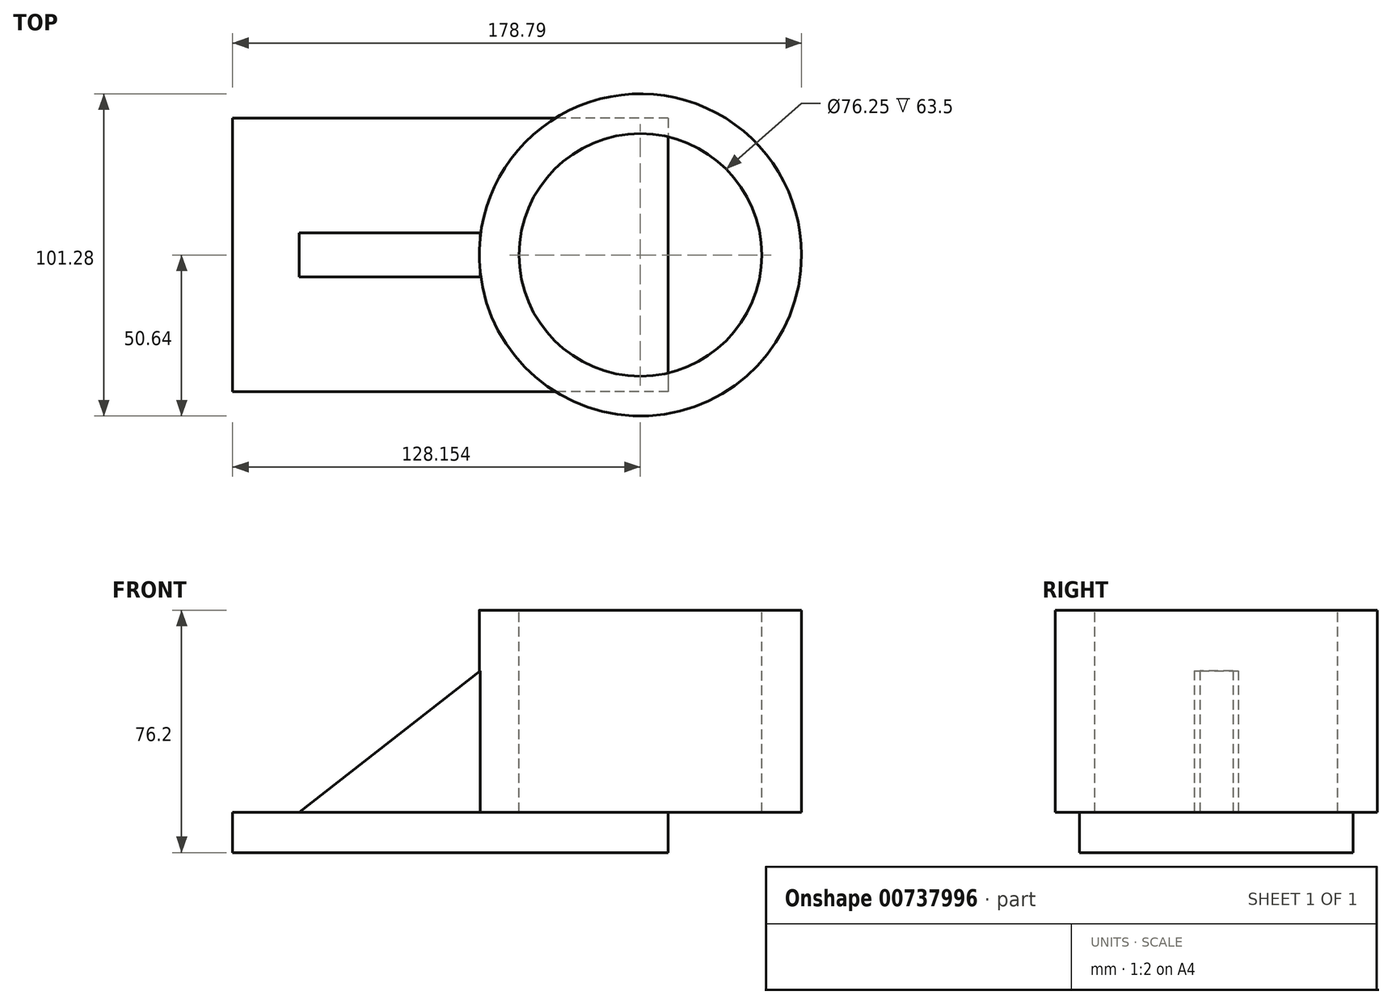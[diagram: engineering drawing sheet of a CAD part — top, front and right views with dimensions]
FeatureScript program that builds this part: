
annotation { "Feature Type Name" : "Feature", "Feature Type Description" : "" }
export const myFeature = defineFeature(function(context is Context, id is Id, definition is map)
    precondition{}
    {
        {
            var Q0;
            Q0=qCreatedBy(makeId("Top.planeOp"),FACE);
            var sketch = newSketch(context, id + "F0", { "sketchPlane" : qUnion([Q0])});
            skLineSegment(sketch, "E0.bottom", {"start": v(68.46, 42.94) * mm, "end": v(-68.46, 42.94) * mm});
            skLineSegment(sketch, "E0.top", {"start": v(68.46, -42.94) * mm, "end": v(-68.46, -42.94) * mm});
            skLineSegment(sketch, "E0.left", {"start": v(68.46, 42.94) * mm, "end": v(68.46, -42.94) * mm});
            skLineSegment(sketch, "E0.right", {"start": v(-68.46, 42.94) * mm, "end": v(-68.46, -42.94) * mm});
            skPoint(sketch, "E0.middle", {"position": v(0, 0) * mm});
            skSolve(sketch);
        }
        {
            var Q0;
            Q0 = qSketchRegion(id + "F0", true);
            extrude(context, id + "F1", {"entities" : qUnion([Q0]), "depth" : 12.7 * mm, "offsetDistance" : 25.4 * mm});
        }
        {
            var Q0;
            Q0=makeQuery(id+"F1.opExtrude","CAP_FACE",FACE,{"disambiguationData":[OSD([sQuery(id+"F0.wireOp",EDGE,"E0.bottom"),sQuery(id+"F0.wireOp",EDGE,"E0.top"),sQuery(id+"F0.wireOp",EDGE,"E0.left"),sQuery(id+"F0.wireOp",EDGE,"E0.right")])],"isStart":false});
            var sketch = newSketch(context, id + "F2", { "sketchPlane" : qUnion([Q0])});
            skCircle(sketch, "E1", {"center": v(59.7, 0) * mm, "radius": 50.64 * mm});
            skPoint(sketch, "E1.centerSnap0", {"position": v(68.46, 0) * mm});
            skSolve(sketch);
        }
        {
            var Q0;
            {var subQ5=makeQuery(id+"F1.opExtrude","CAP_EDGE",EDGE,{"disambiguationData":[OSD([sQuery(id+"F0.wireOp",EDGE,"E0.left")])],"isStart":false});Q0=makeQuery(id+"F2.imprint","IMPRINT",FACE,{"disambiguationData":[TD([[makeQuery(id+"F2.imprint","IMPRINT",EDGE,{"derivedFrom":subQ5}),1.0]])]});}
            var Q1;
            {var subQ5=makeQuery(id+"F1.opExtrude","CAP_EDGE",EDGE,{"disambiguationData":[OSD([sQuery(id+"F0.wireOp",EDGE,"E0.left")])],"isStart":false});Q1=makeQuery(id+"F2.imprint","IMPRINT",FACE,{"disambiguationData":[TD([[makeQuery(id+"F2.imprint","IMPRINT",EDGE,{"derivedFrom":subQ5}),-1.0]])]});}
            extrude(context, id + "F3", {"entities" : qUnion([Q0, Q1]), "operationType" : NewBodyOperationType.ADD, "depth" : 63.5 * mm, "offsetDistance" : 25.4 * mm});
        }
        {
            var Q0;
            Q0=makeQuery(id+"F3.opExtrude","CAP_FACE",FACE,{"disambiguationData":[OSD([sQuery(id+"F2.wireOp",EDGE,"E1")])],"isStart":false});
            var sketch = newSketch(context, id + "F4", { "sketchPlane" : qUnion([Q0])});
            skCircle(sketch, "E2", {"center": v(59.7, 0) * mm, "radius": 38.12 * mm});
            skSolve(sketch);
        }
        {
            var Q0;
            Q0 = qSketchRegion(id + "F4", true);
            extrude(context, id + "F5", {"entities" : qUnion([Q0]), "operationType" : NewBodyOperationType.REMOVE, "oppositeDirection" : true, "depth" : 63.5 * mm, "offsetDistance" : 25.4 * mm});
        }
        {
            var Q0;
            Q0=makeQuery(id+"F1.opExtrude","CAP_FACE",FACE,{"disambiguationData":[OSD([sQuery(id+"F0.wireOp",EDGE,"E0.bottom"),sQuery(id+"F0.wireOp",EDGE,"E0.top"),sQuery(id+"F0.wireOp",EDGE,"E0.left"),sQuery(id+"F0.wireOp",EDGE,"E0.right")])],"isStart":false});
            var sketch = newSketch(context, id + "F6", { "sketchPlane" : qUnion([Q0])});
            skLineSegment(sketch, "E3.bottom", {"start": v(-47.58, -6.98) * mm, "end": v(9.33, -6.98) * mm});
            skLineSegment(sketch, "E3.top", {"start": v(-47.58, 6.98) * mm, "end": v(9.33, 6.98) * mm});
            skLineSegment(sketch, "E3.left", {"start": v(-47.58, -6.98) * mm, "end": v(-47.58, 6.98) * mm});
            skLineSegment(sketch, "E3.right", {"start": v(9.33, -6.98) * mm, "end": v(9.33, 6.98) * mm});
            skPoint(sketch, "E3.middle", {"position": v(-19.13, 0) * mm});
            skSolve(sketch);
        }
        {
            var Q0;
            Q0 = qSketchRegion(id + "F6", true);
            extrude(context, id + "F7", {"entities" : qUnion([Q0]), "operationType" : NewBodyOperationType.ADD, "depth" : 44.45 * mm, "offsetDistance" : 25.4 * mm});
        }
        {
            var Q0;
            Q0=makeQuery(id+"F7.opExtrude","SWEPT_FACE",FACE,{"disambiguationData":[OSD([sQuery(id+"F6.wireOp",EDGE,"E3.top")])]});
            var sketch = newSketch(context, id + "F8", { "sketchPlane" : qUnion([Q0])});
            skLineSegment(sketch, "E4", {"start": v(-9.33, 57.15) * mm, "end": v(47.58, 12.7) * mm});
            skSolve(sketch);
        }
        {
            var Q0;
            Q0=makeQuery(id+"F8.imprint","IMPRINT",FACE,{"disambiguationData":[TD([[makeQuery(id+"F8.imprint","IMPRINT",EDGE,{"derivedFrom":sQuery(id+"F8.wireOp",EDGE,"E4")}),1.0]])]});
            extrude(context, id + "F9", {"entities" : qUnion([Q0]), "operationType" : NewBodyOperationType.REMOVE, "oppositeDirection" : true, "depth" : 25.4 * mm, "offsetDistance" : 25.4 * mm});
        }
    });
